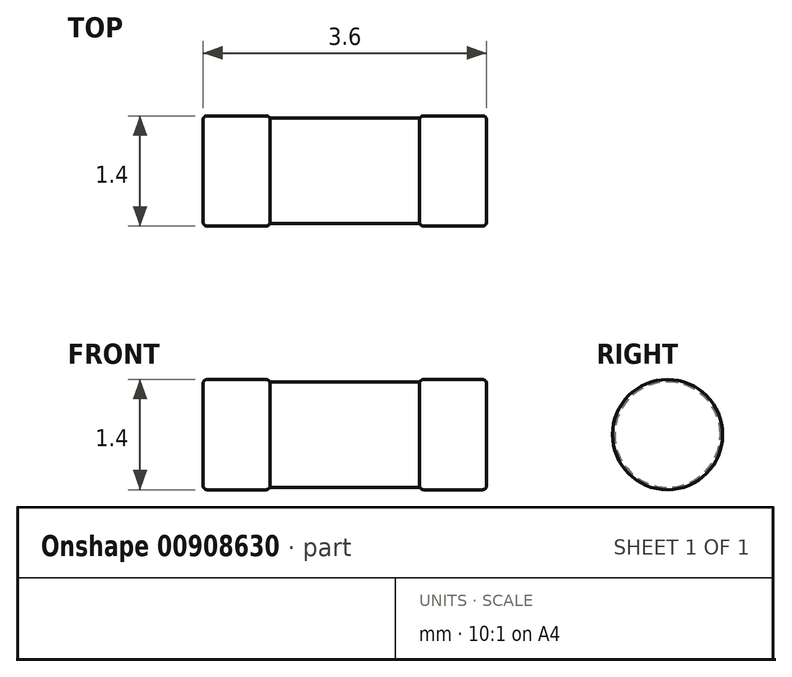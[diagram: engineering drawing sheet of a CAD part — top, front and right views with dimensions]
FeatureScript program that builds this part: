
annotation { "Feature Type Name" : "Feature", "Feature Type Description" : "" }
export const myFeature = defineFeature(function(context is Context, id is Id, definition is map)
    precondition{}
    {
        {
            var Q0;
            Q0=qCreatedBy(makeId("Right.planeOp"),FACE);
            var sketch = newSketch(context, id + "F0", { "sketchPlane" : qUnion([Q0])});
            skCircle(sketch, "E0", {"center": v(0, 0) * mm, "radius": 0.67 * mm});
            skSolve(sketch);
        }
        {
            var Q0;
            Q0=makeQuery(id+"F0.imprint","IMPRINT",FACE,{"disambiguationData":[TD([[makeQuery(id+"F0.imprint","IMPRINT",EDGE,{"derivedFrom":sQuery(id+"F0.wireOp",EDGE,"E0")}),1.0]])]});
            extrude(context, id + "F1", {"entities" : qUnion([Q0]), "endBound" : BoundingType.SYMMETRIC, "depth" : 1.9 * mm, "offsetDistance" : 25 * mm});
        }
        {
            var Q0;
            Q0=makeQuery(id+"F1.opExtrude","CAP_FACE",FACE,{"disambiguationData":[OSD([sQuery(id+"F0.wireOp",EDGE,"E0")])],"isStart":true});
            var sketch = newSketch(context, id + "F2", { "sketchPlane" : qUnion([Q0])});
            skCircle(sketch, "E1", {"center": v(0, 0) * mm, "radius": 0.7 * mm});
            skSolve(sketch);
        }
        {
            var Q0;
            Q0 = qSketchRegion(id + "F2", true);
            var Q1;
            Q1=sQuery(id+"F2.wireOp",EDGE,"E1");
            extrude(context, id + "F3", {"entities" : qUnion([Q0]), "surfaceEntities" : qUnion([Q1]), "depth" : 0.85 * mm, "offsetDistance" : 25 * mm});
        }
        {
            var Q0;
            Q0=makeQuery(id+"F3.opExtrude","CAP_FACE",FACE,{"disambiguationData":[OSD([sQuery(id+"F2.wireOp",EDGE,"E1")])],"isStart":false});
            var Q1;
            Q1=makeQuery(id+"F3.opExtrude","CAP_FACE",FACE,{"disambiguationData":[OSD([sQuery(id+"F2.wireOp",EDGE,"E1")])],"isStart":true});
            fillet(context, id + "F4", {"entities" : qUnion([Q0, Q1]), "radius" : 0.05 * mm, "tangentPropagation" : true, "allowEdgeOverflow" : false});
        }
        {
            var Q0;
            Q0=makeQuery(id+"F3.opExtrude","SWEPT_BODY",BODY,{"disambiguationData":[OSD([sQuery(id+"F2.wireOp",EDGE,"E1")])]});
            var Q1;
            Q1=qCreatedBy(makeId("Right.planeOp"),FACE);
            mirror(context, id + "F5", {"entities" : qUnion([Q0]), "mirrorPlane" : qUnion([Q1])});
        }
    });
